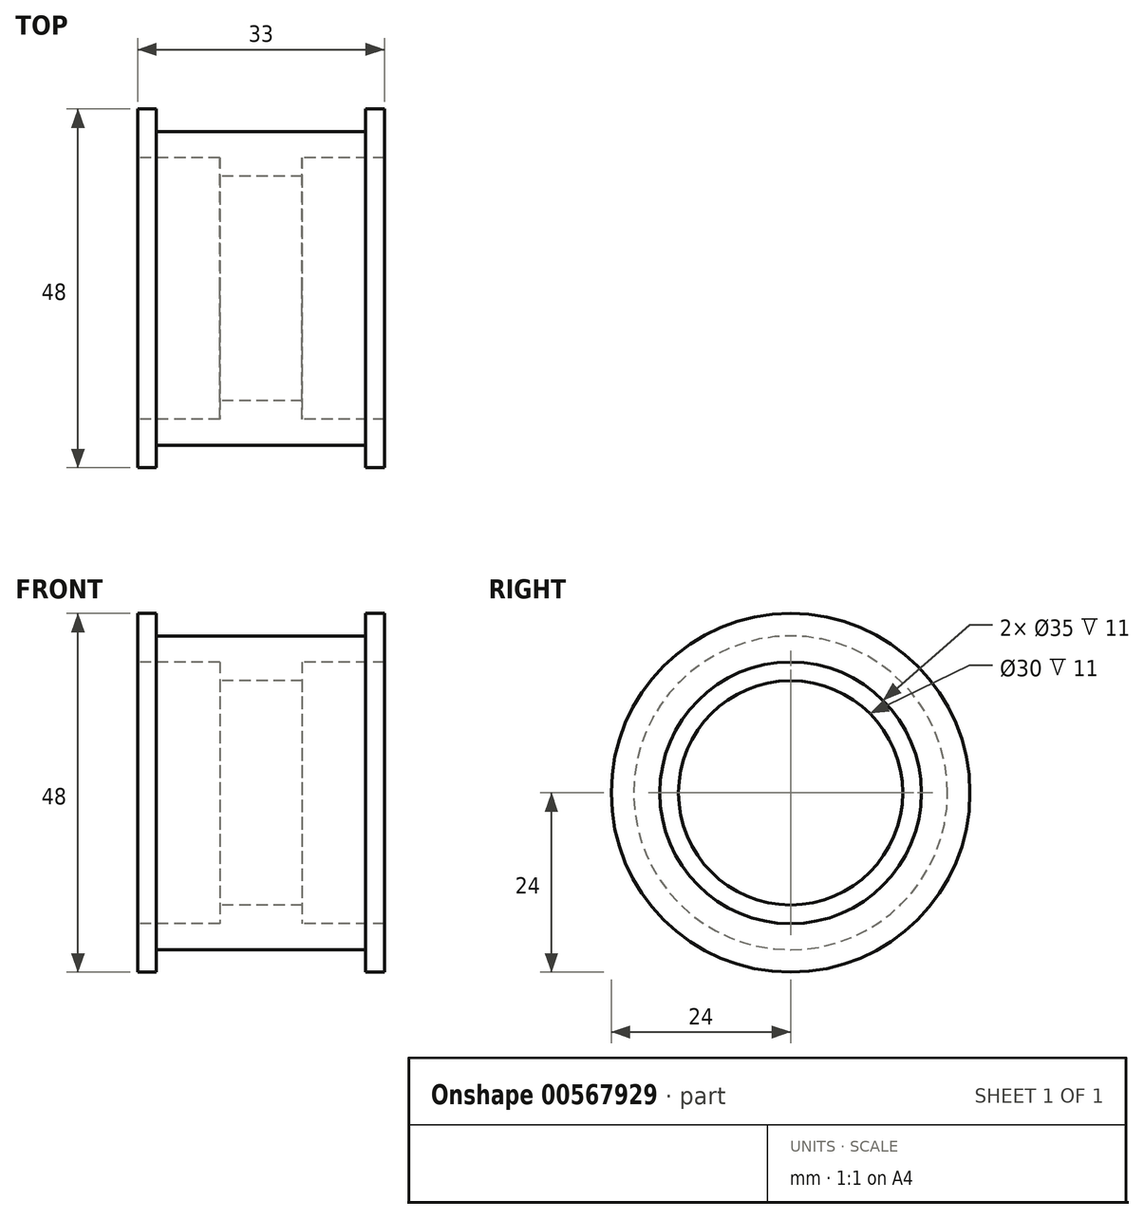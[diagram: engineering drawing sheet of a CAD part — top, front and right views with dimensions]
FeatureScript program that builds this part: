
annotation { "Feature Type Name" : "Feature", "Feature Type Description" : "" }
export const myFeature = defineFeature(function(context is Context, id is Id, definition is map)
    precondition{}
    {
        {
            var Q0;
            Q0=qCreatedBy(makeId("Front.planeOp"),FACE);
            var sketch = newSketch(context, id + "F0", { "sketchPlane" : qUnion([Q0])});
            skLineSegment(sketch, "E0", {"start": v(0, 0) * mm, "end": v(0, -24) * mm});
            skLineSegment(sketch, "E1", {"start": v(0, -24) * mm, "end": v(2.5, -24) * mm});
            skLineSegment(sketch, "E2", {"start": v(2.5, -24) * mm, "end": v(2.5, -21) * mm});
            skLineSegment(sketch, "E3", {"start": v(2.5, -21) * mm, "end": v(30.5, -21) * mm});
            skLineSegment(sketch, "E4", {"start": v(30.5, -21) * mm, "end": v(30.5, -24) * mm});
            skLineSegment(sketch, "E5", {"start": v(30.5, -24) * mm, "end": v(33, -24) * mm});
            skLineSegment(sketch, "E6", {"start": v(33, -24) * mm, "end": v(33, -17.5) * mm});
            skLineSegment(sketch, "E7", {"start": v(33, -17.5) * mm, "end": v(22, -17.5) * mm});
            skLineSegment(sketch, "E8", {"start": v(22, -17.5) * mm, "end": v(22, -15) * mm});
            skLineSegment(sketch, "E9", {"start": v(22, -15) * mm, "end": v(11, -15) * mm});
            skLineSegment(sketch, "E10", {"start": v(11, -15) * mm, "end": v(11, -17.5) * mm});
            skLineSegment(sketch, "E11", {"start": v(11, -17.5) * mm, "end": v(0, -17.5) * mm});
            skLineSegment(sketch, "E12", {"start": v(0, 0) * mm, "end": v(47.97, 0) * mm});
            skSolve(sketch);
        }
        {
            var Q0;
            Q0 = qSketchRegion(id + "F0", true);
            var Q1;
            Q1=sQuery(id+"F0.wireOp",EDGE,"E12");
            revolve(context, id + "F1", {"entities" : qUnion([Q0]), "axis" : qUnion([Q1]), "revolveType" : RevolveType.FULL});
        }
    });
